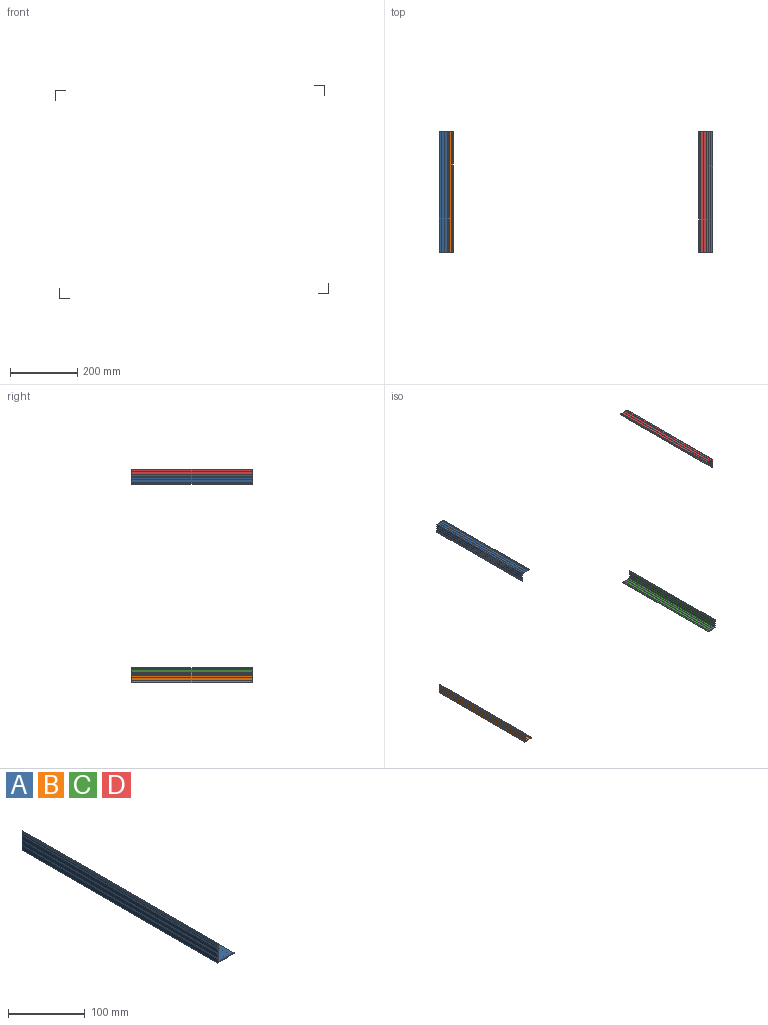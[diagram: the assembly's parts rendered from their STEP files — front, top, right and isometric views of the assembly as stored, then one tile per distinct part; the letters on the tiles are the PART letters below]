
ASSEMBLY  parts=4 mates=3
PART A: 34 faces, bbox 30x360x30 mm
  f0: plane 360x7mm, normal (0,0,-1), area 2520mm2, adj f1,f29,f30,f31
  f1: plane 360x0.49mm, normal (1,0,0), area 175.9mm2, adj f0,f2,f30,f31
  f2: plane 360x1mm, normal (0.01,0,-1), area 360mm2, adj f1,f3,f30,f31
  f3: plane 360x0.5mm, normal (-1,0,-0.01), area 180mm2, adj f2,f4,f30,f31
  f4: plane 360x3.38mm, normal (0,0,-1), area 1217.5mm2, adj f3,f30,f31,f33
  f5: plane 360x0.8mm, normal (1,0,0), area 288mm2, adj f6,f30,f31,f33
  f6: plane 360x28.5mm, normal (0,0,1), area 10260mm2, adj f5,f7,f30,f31
  f7: plane 360x28.5mm, normal (1,0,0), area 10260mm2, adj f6,f8,f30,f31
  f8: plane 360x0.7mm, normal (0,0,1), area 250.6mm2, adj f7,f30,f31,f32
  f9: plane 360x3mm, normal (-1,0,0), area 1080mm2, adj f10,f30,f31,f32
  f10: plane 360x0.5mm, normal (0,0,-1), area 180mm2, adj f9,f11,f30,f31
  f11: plane 360x1mm, normal (-1,0,0), area 360mm2, adj f10,f12,f30,f31
  f12: plane 360x0.5mm, normal (0,0,1), area 180mm2, adj f11,f13,f30,f31
  f13: plane 360x7mm, normal (-1,0,0), area 2520mm2, adj f12,f14,f30,f31
  f14: plane 360x0.5mm, normal (0,0,-1), area 180mm2, adj f13,f15,f30,f31
  f15: plane 360x1mm, normal (-1,0,0), area 360mm2, adj f14,f16,f30,f31
  f16: plane 360x0.5mm, normal (0,0,1), area 180mm2, adj f15,f17,f30,f31
  f17: plane 360x7mm, normal (-1,0,0), area 2520mm2, adj f16,f18,f30,f31
  f18: plane 360x0.5mm, normal (0,0,-1), area 180mm2, adj f17,f19,f30,f31
  f19: plane 360x1mm, normal (-1,0,0), area 360mm2, adj f18,f20,f30,f31
  f20: plane 360x0.5mm, normal (0,0,1), area 180mm2, adj f19,f21,f30,f31
  f21: plane 360x7mm, normal (-1,0,0), area 2520mm2, adj f20,f22,f30,f31
  f22: plane 360x7mm, normal (0,0,-1), area 2520mm2, adj f21,f23,f30,f31
  f23: plane 360x0.5mm, normal (1,0,0), area 180mm2, adj f22,f24,f30,f31
  f24: plane 360x1mm, normal (0,0,-1), area 360mm2, adj f23,f25,f30,f31
  f25: plane 360x0.5mm, normal (-1,0,0), area 180mm2, adj f24,f26,f30,f31
  f26: plane 360x7mm, normal (0,0,-1), area 2520mm2, adj f25,f27,f30,f31
  f27: plane 360x0.5mm, normal (1,0,0), area 180mm2, adj f26,f28,f30,f31
  f28: plane 360x1mm, normal (0,0,-1), area 360mm2, adj f27,f29,f30,f31
  f29: plane 360x0.5mm, normal (-1,0,0), area 180mm2, adj f0,f28,f30,f31
  f30: plane 30x30mm, normal (0,-1,0), area 82.6mm2, adj f0,f1,f2,f3,f4,f5,f6,f7
  f31: plane 30x30mm, normal (0,1,0), area 82.6mm2, adj f0,f1,f2,f3,f4,f5,f6,f7
  f32: plane 360x3mm, normal (-0.97,0,0.26), area 1118.1mm2, adj f8,f9,f30,f31
  f33: plane 360x2.61mm, normal (0.26,0,-0.97), area 973.7mm2, adj f4,f5,f30,f31
PART B: same geometry as A
PART C: same geometry as A
PART D: same geometry as A
PLACE A rot(axis=(0,1,0),88.9deg) t=(-177.57,76.11,970.32)mm
PLACE B rot(axis=(0,-1,0),1.1deg) t=(-165.62,76.11,349.44)mm
PLACE C rot(axis=(0,-1,0),91.1deg) t=(637.23,76.11,364.89)mm
PLACE D rot(axis=(0,1,0),178.9deg) t=(625.28,76.11,985.77)mm
MATE planar B.f30 <-> A.f30  axis (0,-1,0) through (-157.83,-283.89,357.44)mm
MATE planar A.f30 <-> D.f30  axis (0,-1,0) through (-169.57,-283.89,962.53)mm
MATE planar C.f30 <-> D.f30  axis (0,-1,0) through (629.23,-283.89,372.68)mm
